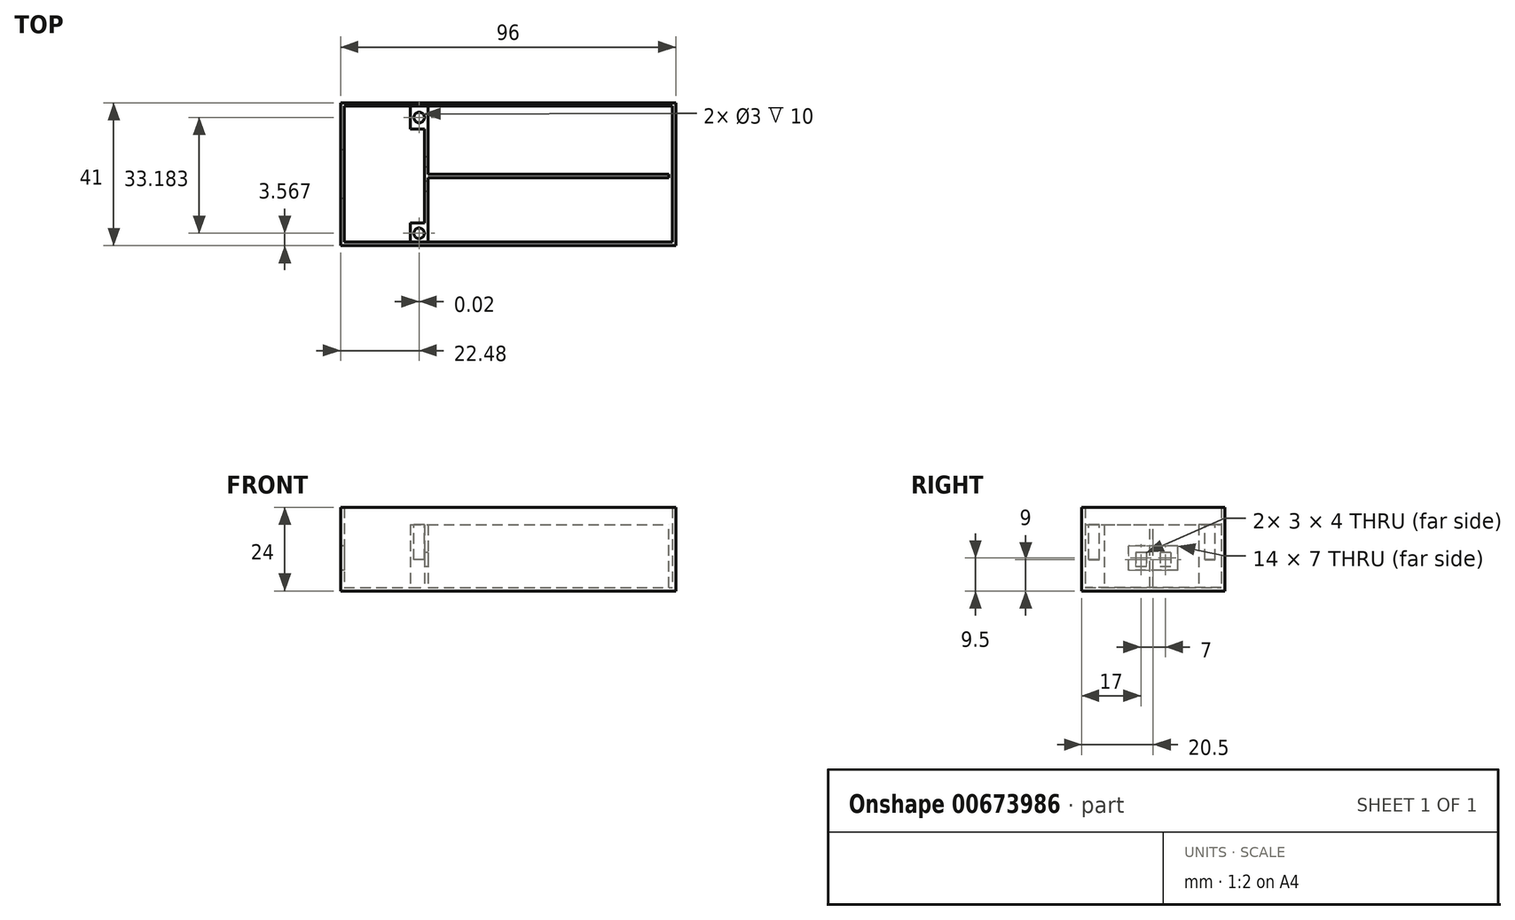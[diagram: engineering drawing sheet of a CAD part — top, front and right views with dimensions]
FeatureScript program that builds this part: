
annotation { "Feature Type Name" : "Feature", "Feature Type Description" : "" }
export const myFeature = defineFeature(function(context is Context, id is Id, definition is map)
    precondition{}
    {
        {
            var Q0;
            Q0=qCreatedBy(makeId("Top.planeOp"),FACE);
            var sketch = newSketch(context, id + "F0", { "sketchPlane" : qUnion([Q0])});
            skLineSegment(sketch, "E0.bottom", {"start": v(-48, 20.5) * mm, "end": v(48, 20.5) * mm});
            skLineSegment(sketch, "E0.top", {"start": v(-48, -20.5) * mm, "end": v(48, -20.5) * mm});
            skLineSegment(sketch, "E0.left", {"start": v(-48, 20.5) * mm, "end": v(-48, -20.5) * mm});
            skLineSegment(sketch, "E0.right", {"start": v(48, 20.5) * mm, "end": v(48, -20.5) * mm});
            skPoint(sketch, "E0.middle", {"position": v(0, 0) * mm});
            skSolve(sketch);
        }
        {
            var Q0;
            Q0=makeQuery(id+"F0.imprint","IMPRINT",FACE,{"disambiguationData":[TD([[makeQuery(id+"F0.imprint","IMPRINT",EDGE,{"derivedFrom":sQuery(id+"F0.wireOp",EDGE,"E0.bottom")}),-1.0]])]});
            extrude(context, id + "F1", {"entities" : qUnion([Q0]), "depth" : 24 * mm, "offsetDistance" : 25 * mm});
        }
        {
            var Q0;
            Q0=makeQuery(id+"F1.opExtrude","CAP_FACE",FACE,{"disambiguationData":[OSD([sQuery(id+"F0.wireOp",EDGE,"E0.bottom"),sQuery(id+"F0.wireOp",EDGE,"E0.top"),sQuery(id+"F0.wireOp",EDGE,"E0.left"),sQuery(id+"F0.wireOp",EDGE,"E0.right")])],"isStart":false});
            shell(context, id + "F2", {"entities" : qUnion([Q0]), "thickness" : 1 * mm});
        }
        {
            var Q0;
            Q0=qCreatedBy(makeId("Front.planeOp"),FACE);
            var sketch = newSketch(context, id + "F3", { "sketchPlane" : qUnion([Q0])});
            skLineSegment(sketch, "E1.bottom", {"start": v(-23, 0) * mm, "end": v(46, 0) * mm});
            skLineSegment(sketch, "E1.top", {"start": v(-23, 19) * mm, "end": v(46, 19) * mm});
            skLineSegment(sketch, "E1.left", {"start": v(-23, 0) * mm, "end": v(-23, 19) * mm});
            skLineSegment(sketch, "E1.right", {"start": v(46, 0) * mm, "end": v(46, 19) * mm});
            skSolve(sketch);
        }
        {
            var Q0;
            Q0=makeQuery(id+"F3.imprint","IMPRINT",FACE,{"disambiguationData":[TD([[makeQuery(id+"F3.imprint","IMPRINT",EDGE,{"derivedFrom":sQuery(id+"F3.wireOp",EDGE,"E1.bottom")}),1.0]])]});
            extrude(context, id + "F4", {"entities" : qUnion([Q0]), "operationType" : NewBodyOperationType.ADD, "depth" : 1 * mm, "offsetDistance" : 25 * mm});
        }
        {
            var Q0;
            Q0=qCreatedBy(makeId("Right.planeOp"),FACE);
            cPlane(context, id + "F5", {"entities" : qUnion([Q0]), "cplaneType" : CPlaneType.OFFSET, "offset" : 24 * mm, "oppositeDirection" : true, "width" : 150 * mm, "height" : 150 * mm});
        }
        {
            var Q0;
            Q0=qCreatedBy(id+"F5.planeOp",FACE);
            var sketch = newSketch(context, id + "F6", { "sketchPlane" : qUnion([Q0])});
            skLineSegment(sketch, "E2.bottom", {"start": v(-14, 19) * mm, "end": v(13, 19) * mm});
            skLineSegment(sketch, "E2.top", {"start": v(-14, 0) * mm, "end": v(13, 0) * mm});
            skLineSegment(sketch, "E2.left", {"start": v(-14, 19) * mm, "end": v(-14, 0) * mm});
            skLineSegment(sketch, "E2.right", {"start": v(13, 19) * mm, "end": v(13, 0) * mm});
            skSolve(sketch);
        }
        {
            var Q0;
            Q0=makeQuery(id+"F6.imprint","IMPRINT",FACE,{"disambiguationData":[TD([[makeQuery(id+"F6.imprint","IMPRINT",EDGE,{"derivedFrom":sQuery(id+"F6.wireOp",EDGE,"E2.bottom")}),-1.0]])]});
            extrude(context, id + "F7", {"entities" : qUnion([Q0]), "operationType" : NewBodyOperationType.ADD, "depth" : 1 * mm, "offsetDistance" : 25 * mm});
        }
        {
            var Q0;
            Q0=makeQuery(id+"F1.opExtrude","SWEPT_FACE",FACE,{"disambiguationData":[OSD([sQuery(id+"F0.wireOp",EDGE,"E0.left")])]});
            var sketch = newSketch(context, id + "F8", { "sketchPlane" : qUnion([Q0])});
            skLineSegment(sketch, "E3.bottom", {"start": v(-7, 6) * mm, "end": v(7, 6) * mm});
            skLineSegment(sketch, "E3.top", {"start": v(-7, 13) * mm, "end": v(7, 13) * mm});
            skLineSegment(sketch, "E3.left", {"start": v(-7, 6) * mm, "end": v(-7, 13) * mm});
            skLineSegment(sketch, "E3.right", {"start": v(7, 6) * mm, "end": v(7, 13) * mm});
            skPoint(sketch, "E3.middle", {"position": v(0, 9.5) * mm});
            skSolve(sketch);
        }
        {
            var Q0;
            Q0=makeQuery(id+"F8.imprint","IMPRINT",FACE,{"disambiguationData":[TD([[makeQuery(id+"F8.imprint","IMPRINT",EDGE,{"derivedFrom":sQuery(id+"F8.wireOp",EDGE,"E3.bottom")}),1.0]])]});
            extrude(context, id + "F9", {"entities" : qUnion([Q0]), "operationType" : NewBodyOperationType.REMOVE, "oppositeDirection" : true, "depth" : 2 * mm, "offsetDistance" : 25 * mm});
        }
        {
            var Q0;
            Q0=makeQuery(id+"F7.opExtrude","CAP_FACE",FACE,{"disambiguationData":[OSD([sQuery(id+"F6.wireOp",EDGE,"E2.bottom"),sQuery(id+"F6.wireOp",EDGE,"E2.top"),sQuery(id+"F6.wireOp",EDGE,"E2.left"),sQuery(id+"F6.wireOp",EDGE,"E2.right")])],"isStart":true});
            var sketch = newSketch(context, id + "F10", { "sketchPlane" : qUnion([Q0])});
            skLineSegment(sketch, "E4.bottom", {"start": v(-5, 11) * mm, "end": v(-2, 11) * mm});
            skLineSegment(sketch, "E4.top", {"start": v(-5, 7) * mm, "end": v(-2, 7) * mm});
            skLineSegment(sketch, "E4.left", {"start": v(-5, 11) * mm, "end": v(-5, 7) * mm});
            skLineSegment(sketch, "E4.right", {"start": v(-2, 11) * mm, "end": v(-2, 7) * mm});
            skLineSegment(sketch, "E5.bottom", {"start": v(2, 11) * mm, "end": v(5, 11) * mm});
            skLineSegment(sketch, "E5.top", {"start": v(2, 7) * mm, "end": v(5, 7) * mm});
            skLineSegment(sketch, "E5.left", {"start": v(2, 11) * mm, "end": v(2, 7) * mm});
            skLineSegment(sketch, "E5.right", {"start": v(5, 11) * mm, "end": v(5, 7) * mm});
            skSolve(sketch);
        }
        {
            var Q0;
            Q0=makeQuery(id+"F10.imprint","IMPRINT",FACE,{"disambiguationData":[TD([[makeQuery(id+"F10.imprint","IMPRINT",EDGE,{"derivedFrom":sQuery(id+"F10.wireOp",EDGE,"E4.bottom")}),-1.0]])]});
            var Q1;
            Q1=makeQuery(id+"F10.imprint","IMPRINT",FACE,{"disambiguationData":[TD([[makeQuery(id+"F10.imprint","IMPRINT",EDGE,{"derivedFrom":sQuery(id+"F10.wireOp",EDGE,"E5.bottom")}),-1.0]])]});
            extrude(context, id + "F11", {"entities" : qUnion([Q0, Q1]), "operationType" : NewBodyOperationType.REMOVE, "oppositeDirection" : true, "depth" : 1 * mm, "offsetDistance" : 25 * mm});
        }
        {
            var Q0;
            Q0=makeQuery(id+"F2.opShell","OFFSET_FACE",FACE,{"disambiguationData":[OSD([sQuery(id+"F0.wireOp",EDGE,"E0.bottom"),sQuery(id+"F0.wireOp",EDGE,"E0.top"),sQuery(id+"F0.wireOp",EDGE,"E0.left"),sQuery(id+"F0.wireOp",EDGE,"E0.right")])]});
            var sketch = newSketch(context, id + "F12", { "sketchPlane" : qUnion([Q0])});
            skLineSegment(sketch, "E6.bottom", {"start": v(-28, 19.5) * mm, "end": v(-23, 19.5) * mm});
            skLineSegment(sketch, "E6.top", {"start": v(-28, 13) * mm, "end": v(-23, 13) * mm});
            skLineSegment(sketch, "E6.left", {"start": v(-28, 19.5) * mm, "end": v(-28, 13) * mm});
            skLineSegment(sketch, "E6.right", {"start": v(-23, 19.5) * mm, "end": v(-23, 13) * mm});
            skLineSegment(sketch, "E7.bottom", {"start": v(-28, -19.5) * mm, "end": v(-23, -19.5) * mm});
            skLineSegment(sketch, "E7.top", {"start": v(-28, -14) * mm, "end": v(-23, -14) * mm});
            skLineSegment(sketch, "E7.left", {"start": v(-28, -19.5) * mm, "end": v(-28, -14) * mm});
            skLineSegment(sketch, "E7.right", {"start": v(-23, -19.5) * mm, "end": v(-23, -14) * mm});
            skSolve(sketch);
        }
        {
            var Q0;
            Q0=makeQuery(id+"F12.imprint","IMPRINT",FACE,{"disambiguationData":[TD([[makeQuery(id+"F12.imprint","IMPRINT",EDGE,{"derivedFrom":sQuery(id+"F12.wireOp",EDGE,"E6.bottom")}),-1.0]])]});
            var Q1;
            Q1=makeQuery(id+"F12.imprint","IMPRINT",FACE,{"disambiguationData":[TD([[makeQuery(id+"F12.imprint","IMPRINT",EDGE,{"derivedFrom":sQuery(id+"F12.wireOp",EDGE,"E7.bottom")}),1.0]])]});
            extrude(context, id + "F13", {"entities" : qUnion([Q0, Q1]), "operationType" : NewBodyOperationType.ADD, "depth" : 18 * mm, "offsetDistance" : 25 * mm});
        }
        {
            var Q0;
            Q0=makeQuery(id+"F13.opExtrude","CAP_FACE",FACE,{"disambiguationData":[OSD([sQuery(id+"F12.wireOp",EDGE,"E6.bottom"),sQuery(id+"F12.wireOp",EDGE,"E6.top"),sQuery(id+"F12.wireOp",EDGE,"E6.left"),sQuery(id+"F12.wireOp",EDGE,"E6.right")])],"isStart":false});
            var sketch = newSketch(context, id + "F14", { "sketchPlane" : qUnion([Q0])});
            skCircle(sketch, "E8", {"center": v(-25.5, 16.25) * mm, "radius": 1.5 * mm});
            skPoint(sketch, "E8.centerSnap0", {"position": v(-25.5, 19.5) * mm});
            skPoint(sketch, "E8.centerSnap1", {"position": v(-28, 16.25) * mm});
            skCircle(sketch, "E9", {"center": v(-25.52, -16.93) * mm, "radius": 1.5 * mm});
            skSolve(sketch);
        }
        {
            var Q0;
            Q0=makeQuery(id+"F14.imprint","IMPRINT",FACE,{"disambiguationData":[TD([[makeQuery(id+"F14.imprint","IMPRINT",EDGE,{"derivedFrom":sQuery(id+"F14.wireOp",EDGE,"E8")}),1.0]])]});
            extrude(context, id + "F15", {"entities" : qUnion([Q0]), "operationType" : NewBodyOperationType.REMOVE, "oppositeDirection" : true, "depth" : 10 * mm, "offsetDistance" : 25 * mm});
        }
        {
            var Q0;
            Q0 = qSketchRegion(id + "F14", true);
            extrude(context, id + "F16", {"entities" : qUnion([Q0]), "operationType" : NewBodyOperationType.REMOVE, "oppositeDirection" : true, "depth" : 10 * mm, "offsetDistance" : 25 * mm});
        }
    });
